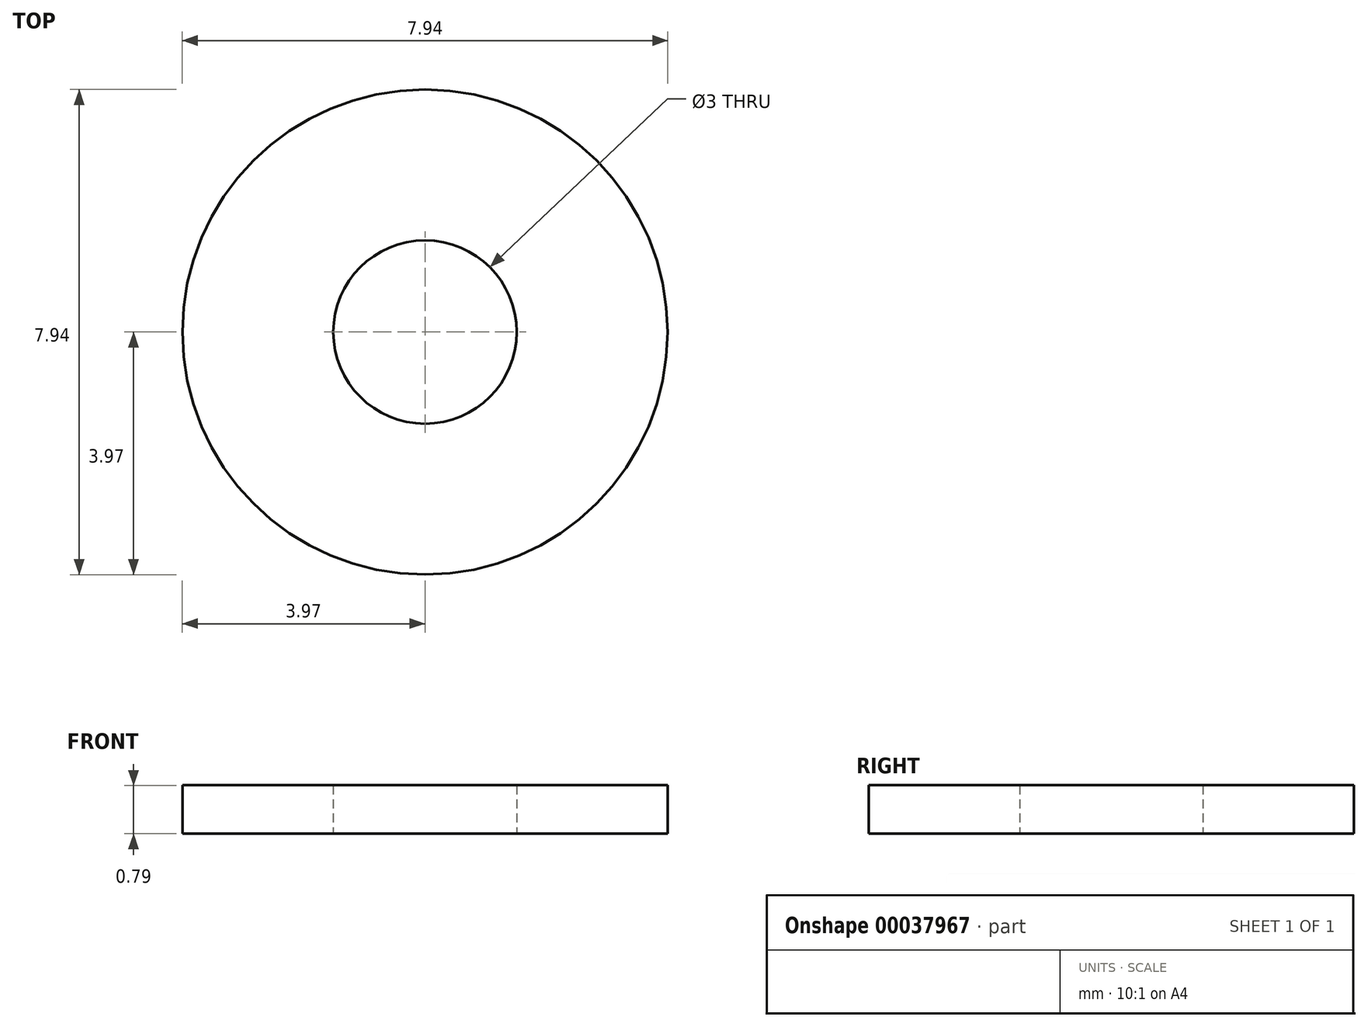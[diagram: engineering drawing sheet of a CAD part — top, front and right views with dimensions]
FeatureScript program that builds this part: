
annotation { "Feature Type Name" : "Feature", "Feature Type Description" : "" }
export const myFeature = defineFeature(function(context is Context, id is Id, definition is map)
    precondition{}
    {
        {
            var Q0;
            Q0=qCreatedBy(makeId("Top.planeOp"),FACE);
            var sketch = newSketch(context, id + "F0", { "sketchPlane" : qUnion([Q0])});
            skCircle(sketch, "E0", {"center": v(0, 0) * mm, "radius": 1.5 * mm});
            skCircle(sketch, "E1", {"center": v(0, 0) * mm, "radius": 3.97 * mm});
            skSolve(sketch);
        }
        {
            var Q0;
            Q0 = qSketchRegion(id + "F0", true);
            extrude(context, id + "F1", {"entities" : qUnion([Q0]), "depth" : 0.8 * mm});
        }
    });
